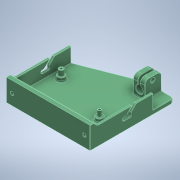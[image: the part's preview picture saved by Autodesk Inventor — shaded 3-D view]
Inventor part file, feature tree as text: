
AUTODESK INVENTOR PART (.ipt)
format: ipt  version: 2021 (Build 250183000, 183)  size: 707,072 bytes
history: native  units: mm
features: fillet x23, sketch x11, reference x11, extrude x10, projected_geometry x8, other x5, hole x3, chamfer x2, plane x1
ambient origin geometry x8: Origin, YZ Plane, XZ Plane, XY Plane, X Axis, Y Axis, Z Axis, Center Point
bodies: Solid1 (feature_tree)
feature tree (74):
  extrude  "Extrusion1"  Depth=110.0mm
  extrude  "Extrusion2"  Depth=6.0mm
  sketch  "Sketch3"  dims[d2=4.0mm d3=0.0mm d4=6.0mm]
  plane  "Work Plane1"
  extrude  "Extrusion3"  Depth=10.0mm
  extrude  "Extrusion4"  Depth=10.0mm
  hole  "Hole2"  [1 undecoded]
  extrude  "Extrusion5"  Depth=10.0mm
  extrude  "Extrusion6"  Depth=6.5mm
  hole  "Hole3"  [1 undecoded]
  extrude  "Extrusion7"  Depth=20.0mm
  hole  "Hole4"  [1 undecoded]
  extrude  "Extrusion9"  Depth=4.5mm TaperAngle=0.0deg
  extrude  "Extrusion10"  Depth=4.5mm TaperAngle=0.0deg
  fillet  "Fillet31"  Radius=8.0mm
  extrude  "Extrusion11"  Depth=4.5mm
  fillet  "Fillet33"  Radius=0.5mm
  chamfer  "Chamfer3"  Distance=0.5mm
  chamfer  "Chamfer4"  Distance=0.5mm
  fillet  "Fillet19"  Radius=0.5mm
  fillet  "Fillet1"  Radius=1.0mm
  fillet  "Fillet2"  Radius=1.0mm
  fillet  "Fillet3"  Radius=1.2mm
  fillet  "Fillet6"  Radius=1.2mm
  fillet  "Fillet8"  Radius=0.5mm
  fillet  "Fillet10"  Radius=0.5mm
  fillet  "Fillet14"  Radius=6.4mm
  fillet  "Fillet15"  Radius=7.6mm
  fillet  "Fillet16"  Radius=23.606152mm
  fillet  "Fillet17"  Radius=39.0mm
  fillet  "Fillet20"  Radius=7.0mm
  fillet  "Fillet21"  Radius=2.5mm
  fillet  "Fillet22"  Radius=7.14375mm
  fillet  "Fillet25"  Radius=2.321875mm
  fillet  "Fillet26"  Radius=2.0mm
  fillet  "Fillet27"  Radius=8.0mm
  fillet  "Fillet29"  Radius=1.0mm
  fillet  "Fillet34"  Radius=0.5mm
  fillet  "Fillet35"  Radius=1.5mm
  fillet  "Fillet36"  Radius=0.3mm
  sketch  "Sketch2"  dims[d0=112.0mm d1=110.0mm]
  reference  "Reference1"
  reference  "Reference2"
  reference  "Reference3"
  sketch  "Sketch5"  dims[d5=25.0mm d6=0.0mm d7=10.0mm]
  sketch  "Sketch7"  dims[d8=10.0mm d9=60.000484mm]
  reference  "Reference7"
  reference  "Reference8"
  reference  "Reference9"
  reference  "Reference10"
  sketch  "Sketch8"  dims[d10=22.4625mm d11=25.0mm d12=0.0mm]
  sketch  "Sketch9"  dims[d20=10.0mm d24=10.0mm]
  reference  "Reference11"
  reference  "Reference12"
  reference  "Reference13"
  reference  "Reference14"
  sketch  "Sketch10"  dims[d25=3.0mm d26=6.5mm]
  projected_geometry  "Projected Loop1"
  projected_geometry  "Projected Loop2"
  sketch  "Sketch11"  dims[d27=6.5mm d28=24.0mm]
  projected_geometry  "Projected Loop3"
  sketch  "Sketch13"  dims[d29=18.0mm d30=0.0mm]
  projected_geometry  "Projected Loop5"
  projected_geometry  "Projected Loop6"
  sketch  "Sketch14"  dims[d31=4.2mm d32=6.0mm d33=5.3mm d34=8.5mm d35=90.0deg d36=8.0mm d37=20.594885mm d38=20.0mm]
  projected_geometry  "Projected Loop7"
  sketch  "Sketch15"  dims[d39=50.0mm d40=4.0mm d41=3.0mm d42=0.0mm d43=3.0mm d44=0.0mm d45=8.0mm d46=8.0mm d47=4.2mm d48=6.0mm d49=4.0mm d50=2.0mm d51=90.0deg d52=8.0mm d53=20.594885mm d60=0.5mm d61=0.5mm d62=0.5mm d65=0.5mm d67=1.0mm d69=1.0mm d73=1.2mm d74=1.2mm d75=0.5mm d76=0.5mm d78=6.4mm d79=7.6mm d80=0.0mm d81=2.5mm d82=6.0mm d83=3.2mm d84=8.0mm d85=90.0deg d86=8.0mm d87=20.594885mm d88=23.606152mm d89=39.0mm d91=7.0mm d92=2.5mm d93=7.14375mm d94=2.321875mm d101=2.0mm d102=0.0mm d104=8.0mm d105=1.0mm d106=2.0mm d107=45.0deg d108=0.5mm d109=2.0mm d110=45.0deg d111=1.5mm d112=0.3mm d113=0.2mm d116=1.0mm d117=0.5mm d118=0.5mm d120=0.5mm d122=9.16875mm d123=20.0mm d125=5.0mm d126=0.0mm d127=11.0mm d128=6.0mm d129=5.0mm d130=0.0mm d132=4.0mm d133=0.5mm d134=0.5mm d135=0.5mm d137=4.5mm]
  projected_geometry  "Projected Loop8"
  projected_geometry  "Projected Loop9"
  other  "FilamentMeasurementAssmV2.iam"
  other  "2780T510FilamentGaugeBearing:3"
  other  "FilamentMeasurementArrmOuter:1"
  other  "2780T510FilamentGaugeBearing:1"
  other  "2780T510FilamentGaugeBearing:2"
note: 3 required parameter values undecoded (feature->parameter linkage not recoverable at this tier; creation-order binding heuristic only, values carry confidence <= 0.55)
